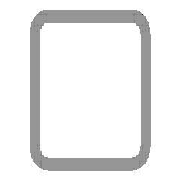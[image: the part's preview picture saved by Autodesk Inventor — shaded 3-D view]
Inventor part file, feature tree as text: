
AUTODESK INVENTOR PART (.ipt)
format: ipt  version: 2025 (Build 290162010, 162A)  size: 142,336 bytes
history: native  units: mm (DEFAULTED — no unit token found)
features: other x4, sketch x1, plane x1
ambient origin geometry x8: Origin, YZ Plane, XZ Plane, XY Plane, X Axis, Y Axis, Z Axis, Center Point
bodies: Solid1 (feature_tree), Body (feature_tree)
feature tree (6):
  parser-record x1  (decoder bookkeeping rows leaked as tree rows — omitted from the tree; the rows remain in map.json)
  other  "Driven Length"
  other  "Start Plane"
  other  "End Plane"
  sketch  "Sketch3"  dims[d3=635.0mm d4=0.0mm d7=4.0mm d9=40.0mm d11=40.0mm d12=2.0mm d13=100.0mm d14=735.0mm d15=20.0mm d16=20.0mm d17=90.0deg d18=635.0mm]
  plane  "Work Plane3"
